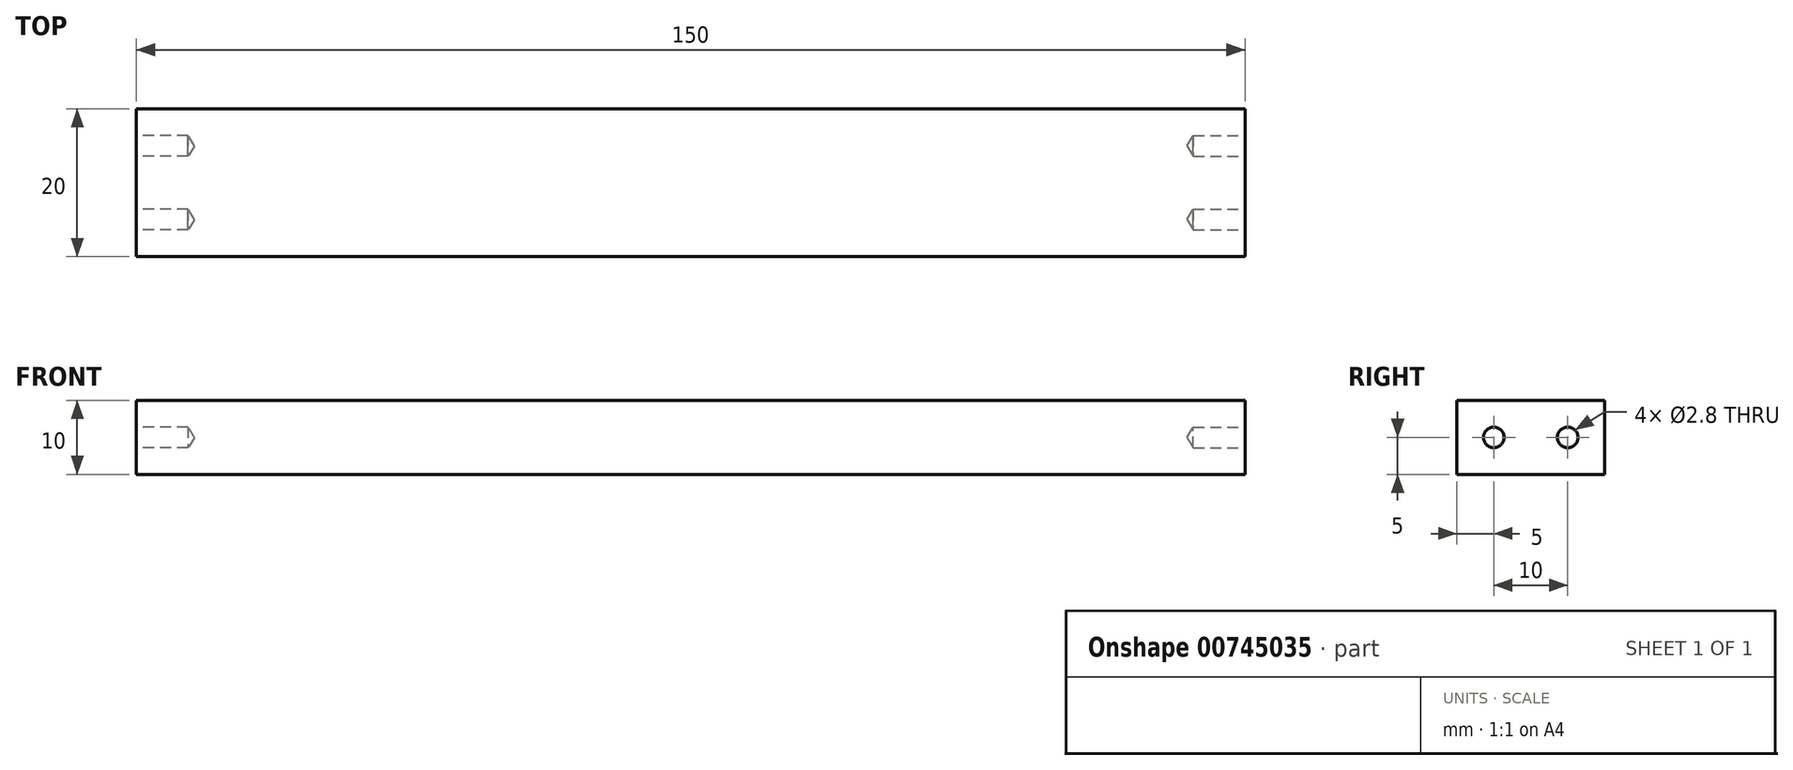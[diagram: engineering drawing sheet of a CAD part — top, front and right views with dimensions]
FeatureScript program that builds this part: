
annotation { "Feature Type Name" : "Feature", "Feature Type Description" : "" }
export const myFeature = defineFeature(function(context is Context, id is Id, definition is map)
    precondition{}
    {
        {
            var Q0;
            Q0=qCreatedBy(makeId("Top.planeOp"),FACE);
            var sketch = newSketch(context, id + "F0", { "sketchPlane" : qUnion([Q0])});
            skLineSegment(sketch, "E0.bottom", {"start": v(75, -10) * mm, "end": v(-75, -10) * mm});
            skLineSegment(sketch, "E0.top", {"start": v(75, 10) * mm, "end": v(-75, 10) * mm});
            skLineSegment(sketch, "E0.left", {"start": v(75, -10) * mm, "end": v(75, 10) * mm});
            skLineSegment(sketch, "E0.right", {"start": v(-75, -10) * mm, "end": v(-75, 10) * mm});
            skPoint(sketch, "E0.middle", {"position": v(0, 0) * mm});
            skSolve(sketch);
        }
        {
            var Q0;
            Q0=makeQuery(id+"F0.imprint","IMPRINT",FACE,{"disambiguationData":[TD([[makeQuery(id+"F0.imprint","IMPRINT",EDGE,{"derivedFrom":sQuery(id+"F0.wireOp",EDGE,"E0.bottom")}),-1.0]])]});
            extrude(context, id + "F1", {"entities" : qUnion([Q0]), "depth" : 10 * mm, "offsetDistance" : 25 * mm});
        }
        {
            var Q0;
            Q0=makeQuery(id+"F1.opExtrude","SWEPT_FACE",FACE,{"disambiguationData":[OSD([sQuery(id+"F0.wireOp",EDGE,"E0.right")])]});
            var sketch = newSketch(context, id + "F2", { "sketchPlane" : qUnion([Q0])});
            skLineSegment(sketch, "E1", {"start": v(-10, 5) * mm, "end": v(10, 5) * mm, "construction": true});
            skPoint(sketch, "E2", {"position": v(-5, 5) * mm});
            skPoint(sketch, "E3", {"position": v(5, 5) * mm});
            skSolve(sketch);
        }
        {
            var Q0;
            Q0=sQuery(id+"F2.wireOp",VERTEX,"E2");
            var Q1;
            Q1=sQuery(id+"F2.wireOp",VERTEX,"E3");
            var Q2;
            Q2=makeQuery(id+"F1.opExtrude","SWEPT_BODY",BODY,{"disambiguationData":[OSD([sQuery(id+"F0.wireOp",EDGE,"E0.bottom"),sQuery(id+"F0.wireOp",EDGE,"E0.top"),sQuery(id+"F0.wireOp",EDGE,"E0.left"),sQuery(id+"F0.wireOp",EDGE,"E0.right")])]});
            hole(context, id + "F3", {"style" : HoleStyle.SIMPLE, "endStyle" : HoleEndStyle.BLIND, "holeDiameter" : 2.8 * mm, "majorDiameter" : 5 * mm, "holeDepth" : 7 * mm, "isTappedThrough" : true, "tappedDepth" : 6 * mm, "tapClearance" : 3, "locations" : qUnion([Q0, Q1]), "scope" : qUnion([Q2])});
        }
        {
            var Q0;
            Q0=makeQuery(id+"F1.opExtrude","SWEPT_FACE",FACE,{"disambiguationData":[OSD([sQuery(id+"F0.wireOp",EDGE,"E0.left")])]});
            var sketch = newSketch(context, id + "F4", { "sketchPlane" : qUnion([Q0])});
            skPoint(sketch, "E4", {"position": v(-5, 5) * mm});
            skPoint(sketch, "E4.positionSnap0", {"position": v(-10, 5) * mm});
            skPoint(sketch, "E5", {"position": v(5, 5) * mm});
            skPoint(sketch, "E5.positionSnap0", {"position": v(10, 5) * mm});
            skSolve(sketch);
        }
        {
            var Q0;
            Q0=sQuery(id+"F4.wireOp",VERTEX,"E4");
            var Q1;
            Q1=sQuery(id+"F4.wireOp",VERTEX,"E5");
            var Q2;
            Q2=makeQuery(id+"F1.opExtrude","SWEPT_BODY",BODY,{"disambiguationData":[OSD([sQuery(id+"F0.wireOp",EDGE,"E0.bottom"),sQuery(id+"F0.wireOp",EDGE,"E0.top"),sQuery(id+"F0.wireOp",EDGE,"E0.left"),sQuery(id+"F0.wireOp",EDGE,"E0.right")])]});
            hole(context, id + "F5", {"style" : HoleStyle.SIMPLE, "endStyle" : HoleEndStyle.BLIND, "holeDiameter" : 2.8 * mm, "majorDiameter" : 5 * mm, "holeDepth" : 7 * mm, "isTappedThrough" : true, "tappedDepth" : 6 * mm, "tapClearance" : 3, "locations" : qUnion([Q0, Q1]), "scope" : qUnion([Q2])});
        }
    });
